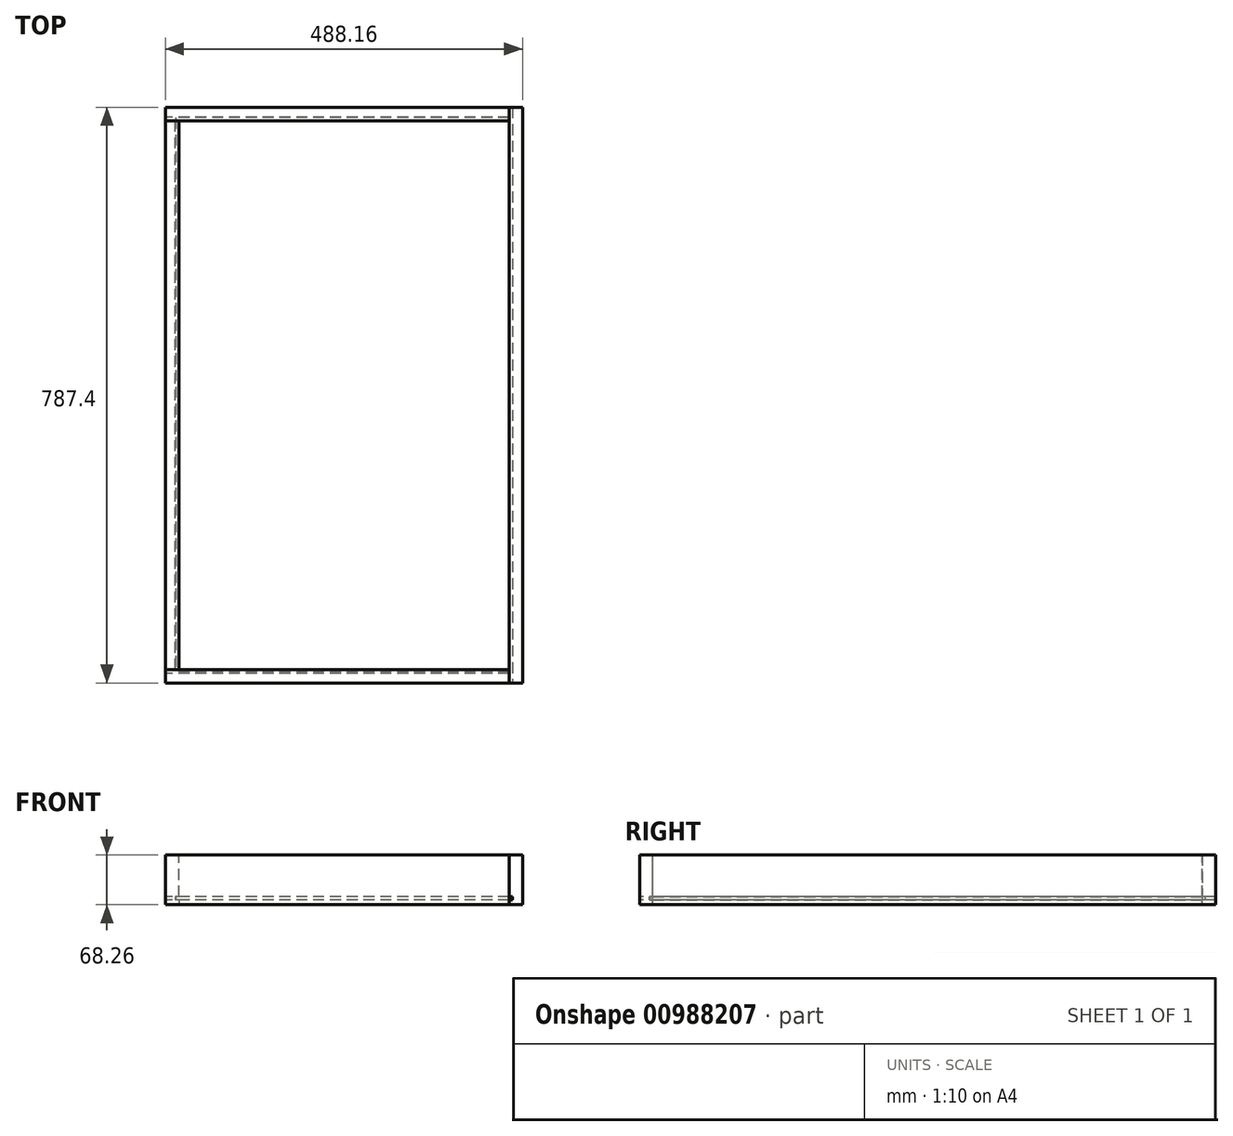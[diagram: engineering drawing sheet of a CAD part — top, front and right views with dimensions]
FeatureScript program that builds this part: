
annotation { "Feature Type Name" : "Feature", "Feature Type Description" : "" }
export const myFeature = defineFeature(function(context is Context, id is Id, definition is map)
    precondition{}
    {
        {
            var Q0;
            Q0=qCreatedBy(makeId("Right.planeOp"),FACE);
            var sketch = newSketch(context, id + "F0", { "sketchPlane" : qUnion([Q0])});
            skLineSegment(sketch, "E0.bottom", {"start": v(393.7, 34.13) * mm, "end": v(-393.7, 34.13) * mm});
            skLineSegment(sketch, "E0.top", {"start": v(393.7, -34.13) * mm, "end": v(-393.7, -34.13) * mm});
            skLineSegment(sketch, "E0.left", {"start": v(393.7, 34.13) * mm, "end": v(393.7, -34.13) * mm});
            skLineSegment(sketch, "E0.right", {"start": v(-393.7, 34.13) * mm, "end": v(-393.7, -34.13) * mm});
            skPoint(sketch, "E0.middle", {"position": v(0, 0) * mm});
            skSolve(sketch);
        }
        {
            var Q0;
            Q0=makeQuery(id+"F0.imprint","IMPRINT",FACE,{"disambiguationData":[TD([[makeQuery(id+"F0.imprint","IMPRINT",EDGE,{"derivedFrom":sQuery(id+"F0.wireOp",EDGE,"E0.bottom")}),1.0]])]});
            extrude(context, id + "F1", {"entities" : qUnion([Q0]), "depth" : 18.26 * mm, "offsetDistance" : 25.4 * mm});
        }
        {
            var Q0;
            Q0=makeQuery(id+"F1.opExtrude","CAP_FACE",FACE,{"disambiguationData":[OSD([sQuery(id+"F0.wireOp",EDGE,"E0.bottom"),sQuery(id+"F0.wireOp",EDGE,"E0.top"),sQuery(id+"F0.wireOp",EDGE,"E0.left"),sQuery(id+"F0.wireOp",EDGE,"E0.right")])],"isStart":true});
            var sketch = newSketch(context, id + "F2", { "sketchPlane" : qUnion([Q0])});
            skLineSegment(sketch, "E1.bottom", {"start": v(393.7, -34.13) * mm, "end": v(375.44, -34.13) * mm});
            skLineSegment(sketch, "E1.top", {"start": v(393.7, 34.13) * mm, "end": v(375.44, 34.13) * mm});
            skLineSegment(sketch, "E1.left", {"start": v(393.7, -34.13) * mm, "end": v(393.7, 34.13) * mm});
            skLineSegment(sketch, "E1.right", {"start": v(375.44, -34.13) * mm, "end": v(375.44, 34.13) * mm});
            skSolve(sketch);
        }
        {
            var Q0;
            Q0=makeQuery(id+"F2.imprint","IMPRINT",FACE,{"disambiguationData":[TD([[makeQuery(id+"F2.imprint","IMPRINT",EDGE,{"derivedFrom":sQuery(id+"F2.wireOp",EDGE,"E1.bottom")}),1.0]])]});
            extrude(context, id + "F3", {"entities" : qUnion([Q0]), "depth" : 469.9 * mm, "offsetDistance" : 25.4 * mm});
        }
        {
            var Q0;
            Q0=makeQuery(id+"F1.opExtrude","SWEPT_FACE",FACE,{"disambiguationData":[OSD([sQuery(id+"F0.wireOp",EDGE,"E0.right")])]});
            var sketch = newSketch(context, id + "F4", { "sketchPlane" : qUnion([Q0])});
            skLineSegment(sketch, "E2.bottom", {"start": v(4.83, -27.78) * mm, "end": v(0, -27.78) * mm});
            skLineSegment(sketch, "E2.top", {"start": v(4.83, -22.96) * mm, "end": v(0, -22.96) * mm});
            skLineSegment(sketch, "E2.left", {"start": v(4.83, -27.78) * mm, "end": v(4.83, -22.96) * mm});
            skLineSegment(sketch, "E2.right", {"start": v(0, -27.78) * mm, "end": v(0, -22.96) * mm});
            skPoint(sketch, "E2.middle", {"position": v(2.41, -25.37) * mm});
            skSolve(sketch);
        }
        {
            var Q0;
            Q0=makeQuery(id+"F4.imprint","IMPRINT",FACE,{"disambiguationData":[TD([[makeQuery(id+"F4.imprint","IMPRINT",EDGE,{"derivedFrom":sQuery(id+"F4.wireOp",EDGE,"E2.bottom")}),-1.0]])]});
            extrude(context, id + "F5", {"entities" : qUnion([Q0]), "operationType" : NewBodyOperationType.REMOVE, "endBound" : BoundingType.THROUGH_ALL, "oppositeDirection" : true, "depth" : 25.4 * mm, "offsetDistance" : 25.4 * mm});
        }
        {
            var Q0;
            Q0=makeQuery(id+"F3.opExtrude","CAP_FACE",FACE,{"disambiguationData":[OSD([sQuery(id+"F2.wireOp",EDGE,"E1.bottom"),sQuery(id+"F2.wireOp",EDGE,"E1.top"),sQuery(id+"F2.wireOp",EDGE,"E1.left"),sQuery(id+"F2.wireOp",EDGE,"E1.right")])],"isStart":false});
            var sketch = newSketch(context, id + "F6", { "sketchPlane" : qUnion([Q0])});
            skLineSegment(sketch, "E3.0", {"start": v(-393.7, -27.78) * mm, "end": v(393.7, -27.78) * mm});
            skLineSegment(sketch, "E4.0", {"start": v(-393.7, -22.96) * mm, "end": v(393.7, -22.96) * mm});
            skLineSegment(sketch, "E5", {"start": v(380.27, -22.96) * mm, "end": v(380.27, -27.78) * mm});
            skSolve(sketch);
        }
        {
            var Q0;
            {var subQ0=sQuery(id+"F6.wireOp",EDGE,"E5");Q0=makeQuery(id+"F6.imprint","IMPRINT",FACE,{"disambiguationData":[TD([[makeQuery(id+"F6.imprint","IMPRINT",EDGE,{"derivedFrom":subQ0}),-1.0]])]});}
            extrude(context, id + "F7", {"entities" : qUnion([Q0]), "operationType" : NewBodyOperationType.REMOVE, "endBound" : BoundingType.UP_TO_NEXT, "oppositeDirection" : true, "depth" : 25.4 * mm, "offsetDistance" : 25.4 * mm});
        }
        {
            var Q0;
            Q0=makeQuery(id+"F3.opExtrude","SWEPT_BODY",BODY,{"disambiguationData":[OSD([sQuery(id+"F2.wireOp",EDGE,"E1.bottom"),sQuery(id+"F2.wireOp",EDGE,"E1.top"),sQuery(id+"F2.wireOp",EDGE,"E1.left"),sQuery(id+"F2.wireOp",EDGE,"E1.right")])]});
            var Q1;
            Q1=qCreatedBy(makeId("Front.planeOp"),FACE);
            mirror(context, id + "F8", {"entities" : qUnion([Q0]), "mirrorPlane" : qUnion([Q1])});
        }
        {
            var Q0;
            {var subQ0=sQuery(id+"F2.wireOp",EDGE,"E1.right");var subQ2=sQuery(id+"F2.wireOp",EDGE,"E1.top");Q0=makeQuery(id+"F7.boolean.opBoolean","SPLIT",FACE,{"disambiguationData":[TD([makeQuery(id+"F3.opExtrude","SWEPT_FACE",FACE,{"disambiguationData":[OSD([subQ2])]})])],"derivedFrom":makeQuery(id+"F3.opExtrude","SWEPT_FACE",FACE,{"disambiguationData":[OSD([subQ0])]})});}
            var sketch = newSketch(context, id + "F9", { "sketchPlane" : qUnion([Q0])});
            skLineSegment(sketch, "E6.bottom", {"start": v(469.9, -34.13) * mm, "end": v(451.64, -34.13) * mm});
            skLineSegment(sketch, "E6.top", {"start": v(469.9, 34.13) * mm, "end": v(451.64, 34.13) * mm});
            skLineSegment(sketch, "E6.left", {"start": v(469.9, -34.13) * mm, "end": v(469.9, 34.13) * mm});
            skLineSegment(sketch, "E6.right", {"start": v(451.64, -34.13) * mm, "end": v(451.64, 34.13) * mm});
            skPoint(sketch, "E6.middle", {"position": v(460.77, 0) * mm});
            skSolve(sketch);
        }
        {
            var Q0;
            Q0 = qSketchRegion(id + "F9", true);
            var Q1;
            {var subQ0=sQuery(id+"F2.wireOp",EDGE,"E1.right");var subQ2=sQuery(id+"F2.wireOp",EDGE,"E1.top");Q1=makeQuery(id+"F8.opPattern","COPY",FACE,{"derivedFrom":makeQuery(id+"F7.boolean.opBoolean","SPLIT",FACE,{"disambiguationData":[TD([makeQuery(id+"F3.opExtrude","SWEPT_FACE",FACE,{"disambiguationData":[OSD([subQ2])]})])],"derivedFrom":makeQuery(id+"F3.opExtrude","SWEPT_FACE",FACE,{"disambiguationData":[OSD([subQ0])]})}),"instanceName":"1"});}
            extrude(context, id + "F10", {"entities" : qUnion([Q0]), "endBound" : BoundingType.UP_TO_SURFACE, "depth" : 25.4 * mm, "endBoundEntityFace" : qUnion([Q1]), "offsetDistance" : 25.4 * mm});
        }
        {
            var Q0;
            Q0=makeQuery(id+"F10.opExtrude","CAP_FACE",FACE,{"disambiguationData":[OSD([sQuery(id+"F9.wireOp",EDGE,"E6.bottom"),sQuery(id+"F9.wireOp",EDGE,"E6.top"),sQuery(id+"F9.wireOp",EDGE,"E6.left"),sQuery(id+"F9.wireOp",EDGE,"E6.right")])],"isStart":false});
            var sketch = newSketch(context, id + "F11", { "sketchPlane" : qUnion([Q0])});
            skLineSegment(sketch, "E7.0", {"start": v(0, -27.78) * mm, "end": v(469.9, -27.78) * mm});
            skLineSegment(sketch, "E8.0", {"start": v(0, -22.96) * mm, "end": v(469.9, -22.96) * mm});
            skLineSegment(sketch, "E9", {"start": v(456.47, -22.96) * mm, "end": v(456.47, -27.78) * mm});
            skSolve(sketch);
        }
        {
            var Q0;
            {var subQ0=sQuery(id+"F11.wireOp",EDGE,"E9");Q0=makeQuery(id+"F11.imprint","IMPRINT",FACE,{"disambiguationData":[TD([[makeQuery(id+"F11.imprint","IMPRINT",EDGE,{"derivedFrom":subQ0}),-1.0]])]});}
            extrude(context, id + "F12", {"entities" : qUnion([Q0]), "operationType" : NewBodyOperationType.REMOVE, "endBound" : BoundingType.UP_TO_NEXT, "oppositeDirection" : true, "depth" : 25.4 * mm, "offsetDistance" : 25.4 * mm});
        }
        {
            var Q0;
            Q0=makeQuery(id+"F5.boolean.opBoolean","COPY",FACE,{"derivedFrom":makeQuery(id+"F5.opExtrude","SWEPT_FACE",FACE,{"disambiguationData":[OSD([sQuery(id+"F4.wireOp",EDGE,"E2.bottom")])]})});
            var sketch = newSketch(context, id + "F13", { "sketchPlane" : qUnion([Q0])});
            skLineSegment(sketch, "E10.0", {"start": v(-469.9, -375.44) * mm, "end": v(0, -375.44) * mm, "construction": true});
            skLineSegment(sketch, "E11.0", {"start": v(-451.64, 375.44) * mm, "end": v(-451.64, -375.44) * mm, "construction": true});
            skLineSegment(sketch, "E12.0", {"start": v(-469.9, 375.44) * mm, "end": v(0, 375.44) * mm, "construction": true});
            skLineSegment(sketch, "E13.0", {"start": v(0, 393.7) * mm, "end": v(0, -393.7) * mm, "construction": true});
            skLineSegment(sketch, "E14.bottom", {"start": v(3.97, 379.41) * mm, "end": v(-455.61, 379.41) * mm});
            skLineSegment(sketch, "E14.top", {"start": v(3.97, -379.41) * mm, "end": v(-455.61, -379.41) * mm});
            skLineSegment(sketch, "E14.left", {"start": v(3.97, 379.41) * mm, "end": v(3.97, -379.41) * mm});
            skLineSegment(sketch, "E14.right", {"start": v(-455.61, 379.41) * mm, "end": v(-455.61, -379.41) * mm});
            skPoint(sketch, "E14.middle", {"position": v(-225.82, 0) * mm});
            skSolve(sketch);
        }
        {
            var Q0;
            {var subQ0=sQuery(id+"F13.wireOp",EDGE,"E14.right");Q0=makeQuery(id+"F13.imprint","IMPRINT",FACE,{"disambiguationData":[TD([[makeQuery(id+"F13.imprint","IMPRINT",EDGE,{"derivedFrom":subQ0}),1.0]])]});}
            extrude(context, id + "F14", {"entities" : qUnion([Q0]), "depth" : 4.76 * mm, "offsetDistance" : 25.4 * mm});
        }
    });
